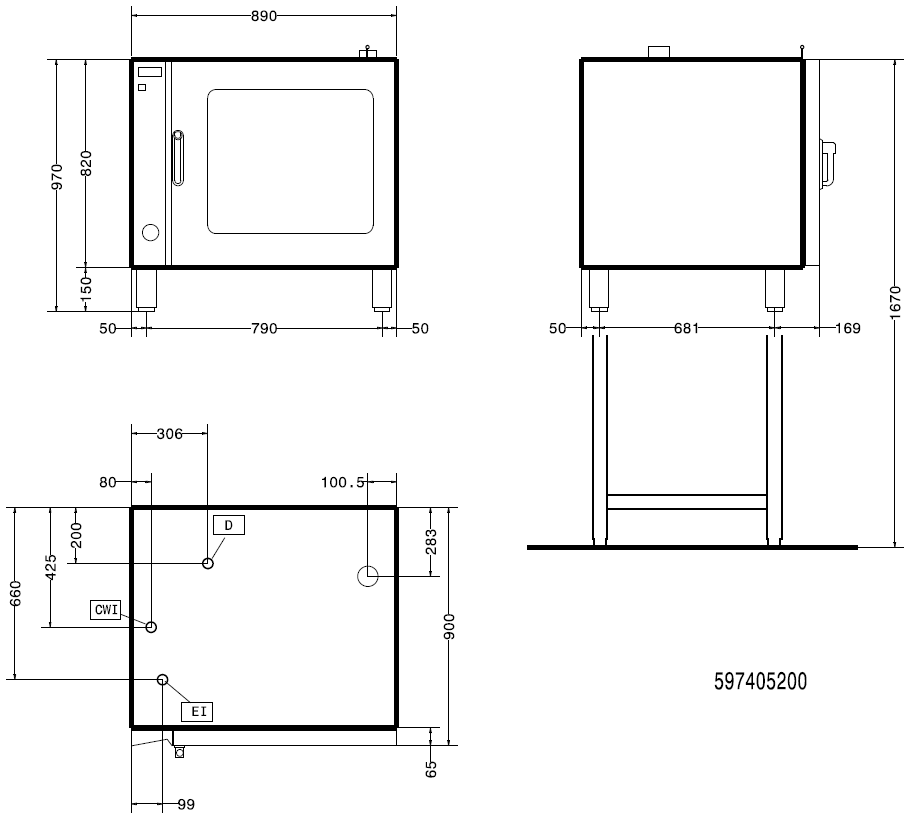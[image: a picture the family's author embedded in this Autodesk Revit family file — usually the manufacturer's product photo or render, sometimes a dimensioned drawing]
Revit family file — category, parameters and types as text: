
# Revit family: QF_ELECTROLUXPROFESSIONAL_260710_ECF202ENS
name_source: partatom
category: Specialty Equipment
revit_build: Autodesk Revit 2018 (Build: 20190510_1515(x64)
units: mm (PartAtom-declared; Revit-internal decimal feet)

## family parameters
Always vertical = Yes
Cut with Voids When Loaded = No
Part Type = Normal
Room Calculation Point = No
Round Connector Dimension = Use Diameter
Shared = No
Work Plane-Based = No

## types (1)
- Standard
    Accessory = Yes
    Cold Water Size = 19 mm
    Compressed Air Pressure = 0.0 Pa
    Compressed Air Size = 0 mm
    Compressed Air Volume = 0.0 L/s
    Condensate Return Size = 0 mm
    Cycle = 60 Hz
    Depth Actual = 1215 mm  [stored 3.98622 ft]
    Description = EL.CONVECTION OVEN 20 GN 2/1,CROSS-WISE-60HZ
    Direct Waste Size = 25 mm
    Gas Input Pressure = 0
    Gas KW = 0
    Gas Size = 0 mm
    HP = 65.6 HP
    Height Actual = 1700 mm  [stored 5.57743 ft]
    Hot Water Size = 0 mm
    Item Number = 260710
    Length Actual = 890 mm  [stored 2.91995 ft]
    Manufacturer = Electrolux Professional
    Model = ECF202ENS
    Phase = 3
    Refrigerant Compressor Remote = Yes
    Refrigeration Liquid Line Size = 0 mm
    Refrigeration Suction Line Size = 0 mm
    Steam Pounds per Hour = 0
    Steam Supply Maximum Pressure = 0.0 Pa
    Steam Supply Minimum Pressure = 0.0 Pa
    Steam Supply Size = 0 mm
    URL = http://professional.electrolux.com
    URL Manufacturer = http://professional.electrolux.com
    Volts = 380 V
    Watts = 0 W
    Weight = 271.40 kg

note: source unit labels omitted for Gas Input Pressure — the stored unit's dimension contradicts the parameter name (converter mislabeling)

note: [stored X ft] marks values corroborated as IEEE doubles in the binary element streams (Revit-internal decimal feet)

## geometry (parser evidence)
native form markers: Sweep x4
no freeform markers — native parametric forms only
